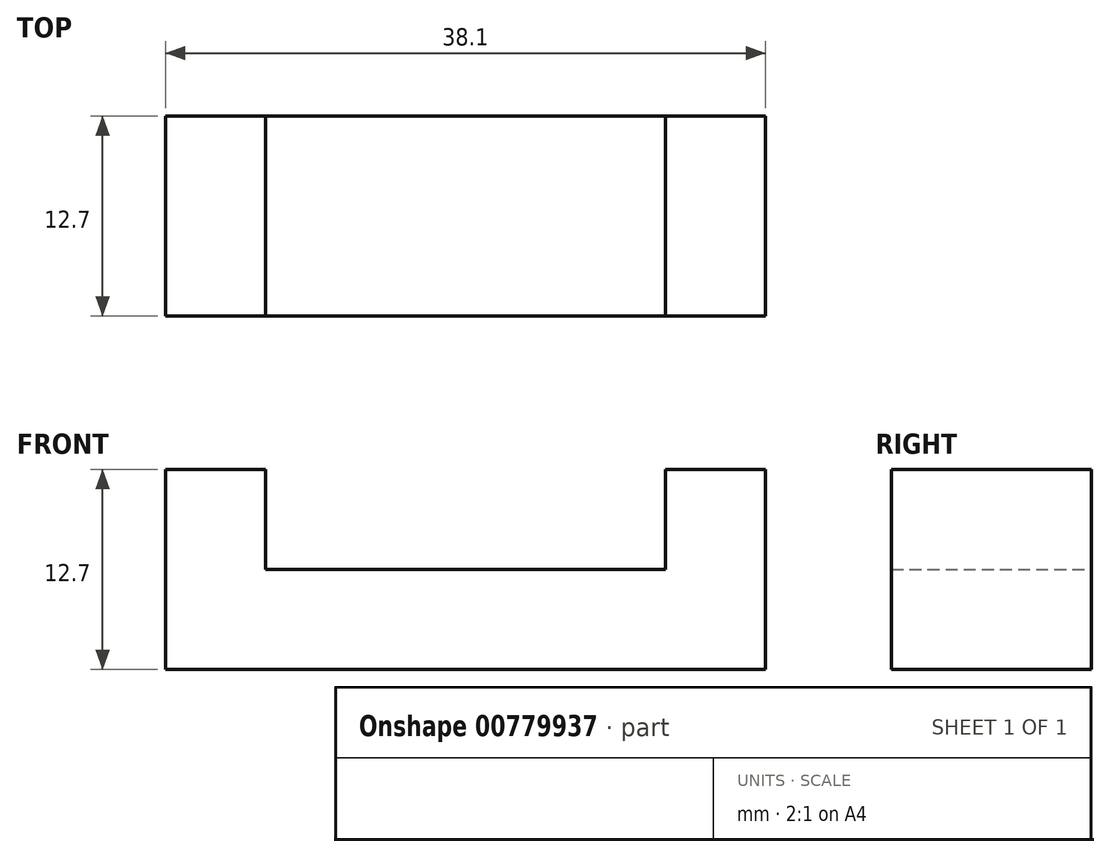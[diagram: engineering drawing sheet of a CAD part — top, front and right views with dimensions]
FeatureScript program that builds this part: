
annotation { "Feature Type Name" : "Feature", "Feature Type Description" : "" }
export const myFeature = defineFeature(function(context is Context, id is Id, definition is map)
    precondition{}
    {
        {
            var Q0;
            Q0=qCreatedBy(makeId("Top.planeOp"),FACE);
            var sketch = newSketch(context, id + "F0", { "sketchPlane" : qUnion([Q0])});
            skLineSegment(sketch, "E0.bottom", {"start": v(0, 0) * mm, "end": v(-38.1, 0) * mm});
            skLineSegment(sketch, "E0.top", {"start": v(0, 12.7) * mm, "end": v(-38.1, 12.7) * mm});
            skLineSegment(sketch, "E0.left", {"start": v(0, 0) * mm, "end": v(0, 12.7) * mm});
            skLineSegment(sketch, "E0.right", {"start": v(-38.1, 0) * mm, "end": v(-38.1, 12.7) * mm});
            skLineSegment(sketch, "E1.bottom", {"start": v(0, 0) * mm, "end": v(-6.35, 0) * mm});
            skLineSegment(sketch, "E1.top", {"start": v(0, 12.7) * mm, "end": v(-6.35, 12.7) * mm});
            skLineSegment(sketch, "E1.right", {"start": v(-6.35, 0) * mm, "end": v(-6.35, 12.7) * mm});
            skLineSegment(sketch, "E2.bottom", {"start": v(-38.1, 0) * mm, "end": v(-31.75, 0) * mm});
            skLineSegment(sketch, "E2.top", {"start": v(-38.1, 12.7) * mm, "end": v(-31.75, 12.7) * mm});
            skLineSegment(sketch, "E2.right", {"start": v(-31.75, 0) * mm, "end": v(-31.75, 12.7) * mm});
            skSolve(sketch);
        }
        {
            var Q0;
            {var subQ0=sQuery(id+"F0.wireOp",EDGE,"E1.right");Q0=makeQuery(id+"F0.imprint","IMPRINT",FACE,{"disambiguationData":[TD([[makeQuery(id+"F0.imprint","IMPRINT",EDGE,{"derivedFrom":subQ0}),1.0]])]});}
            extrude(context, id + "F1", {"entities" : qUnion([Q0]), "depth" : 6.35 * mm, "offsetDistance" : 25.4 * mm});
        }
        {
            var Q0;
            {var subQ2=sQuery(id+"F0.wireOp",EDGE,"E0.left");Q0=makeQuery(id+"F0.imprint","IMPRINT",FACE,{"disambiguationData":[TD([[makeQuery(id+"F0.imprint","IMPRINT",EDGE,{"derivedFrom":subQ2}),1.0]])]});}
            var Q1;
            {var subQ0=sQuery(id+"F0.wireOp",EDGE,"E0.right");Q1=makeQuery(id+"F0.imprint","IMPRINT",FACE,{"disambiguationData":[TD([[makeQuery(id+"F0.imprint","IMPRINT",EDGE,{"derivedFrom":subQ0}),-1.0]])]});}
            extrude(context, id + "F2", {"entities" : qUnion([Q0, Q1]), "operationType" : NewBodyOperationType.ADD, "depth" : 12.7 * mm, "offsetDistance" : 25.4 * mm});
        }
    });
